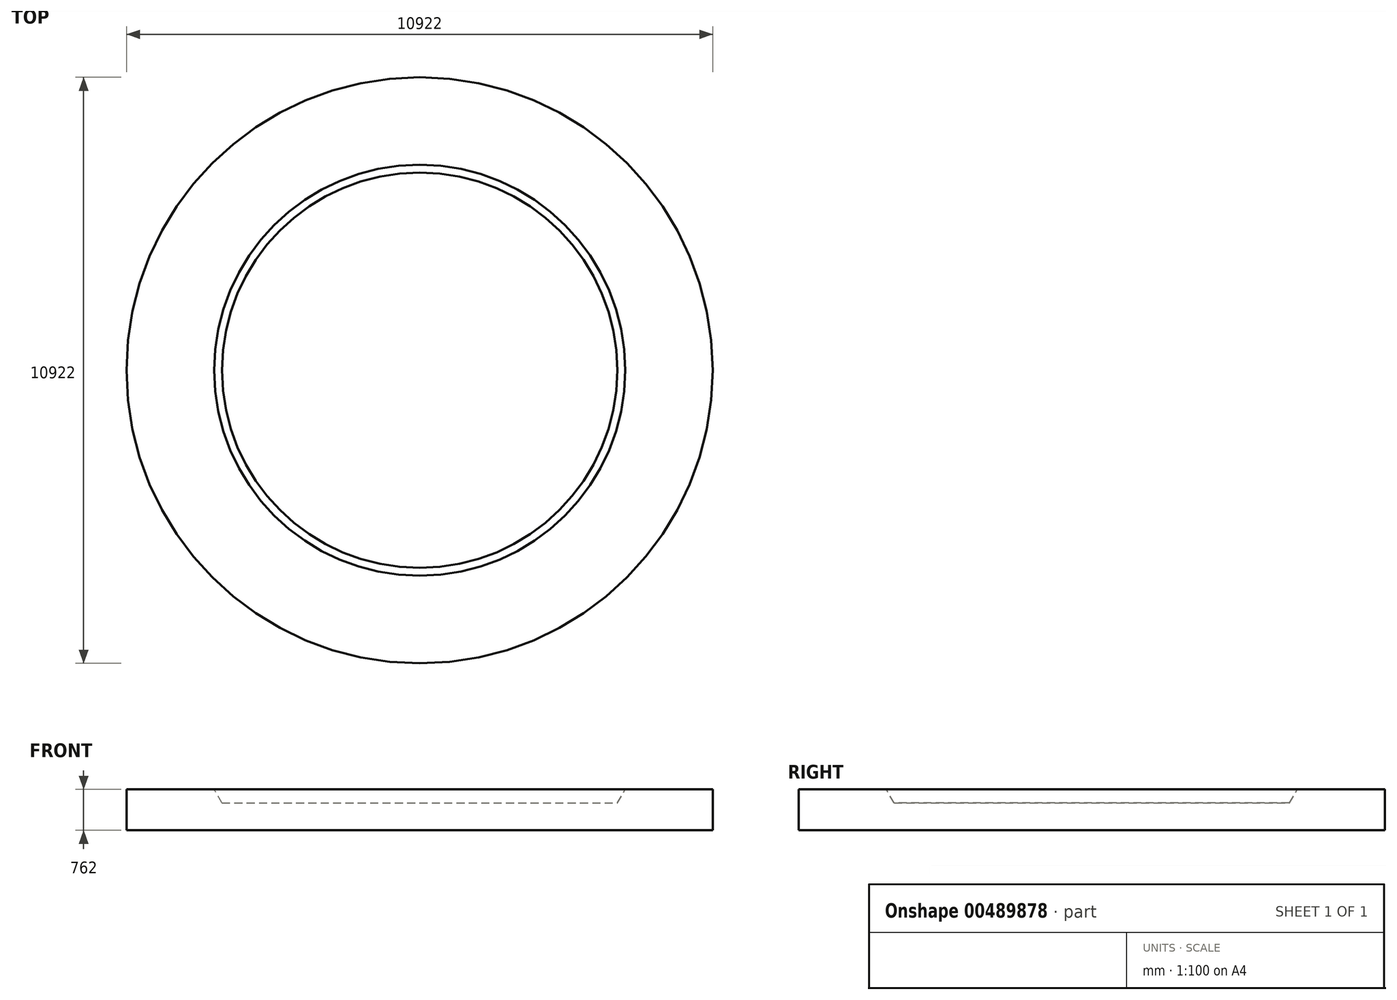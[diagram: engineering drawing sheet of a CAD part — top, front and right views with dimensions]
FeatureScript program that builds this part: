
annotation { "Feature Type Name" : "Feature", "Feature Type Description" : "" }
export const myFeature = defineFeature(function(context is Context, id is Id, definition is map)
    precondition{}
    {
        {
            var Q0;
            Q0=qCreatedBy(makeId("Front.planeOp"),FACE);
            var sketch = newSketch(context, id + "F0", { "sketchPlane" : qUnion([Q0])});
            skLineSegment(sketch, "E0.bottom", {"start": v(-5461, 0) * mm, "end": v(0, 0) * mm});
            skLineSegment(sketch, "E0.top", {"start": v(-5461, -762) * mm, "end": v(0, -762) * mm});
            skLineSegment(sketch, "E0.left", {"start": v(-5461, 0) * mm, "end": v(-5461, -762) * mm});
            skLineSegment(sketch, "E1", {"start": v(0, 0) * mm, "end": v(0, -762) * mm});
            skPoint(sketch, "E0.right.end.orphan", {"position": v(5461, -762) * mm});
            skLineSegment(sketch, "E2", {"start": v(0, -254) * mm, "end": v(-3683, -254) * mm});
            skLineSegment(sketch, "E3", {"start": v(0, -61.85) * mm, "end": v(0, 51.67) * mm, "construction": true});
            skLineSegment(sketch, "E4", {"start": v(-6.7, 2290.73) * mm, "end": v(13.22, 2290.73) * mm, "construction": true});
            skLineSegment(sketch, "E5", {"start": v(-3683, -254) * mm, "end": v(-3829.65, 0) * mm});
            skLineSegment(sketch, "E6", {"start": v(-3829.65, 0) * mm, "end": v(-3683, -254) * mm});
            skSolve(sketch);
        }
        {
            var Q0;
            {var subQ1=sQuery(id+"F0.wireOp",EDGE,"E0.top");Q0=makeQuery(id+"F0.imprint","IMPRINT",FACE,{"disambiguationData":[TD([[makeQuery(id+"F0.imprint","IMPRINT",EDGE,{"derivedFrom":subQ1}),1.0]])]});}
            var Q1;
            Q1=sQuery(id+"F0.wireOp",EDGE,"E3");
            revolve(context, id + "F1", {"entities" : qUnion([Q0]), "axis" : qUnion([Q1]), "revolveType" : RevolveType.FULL});
        }
    });
